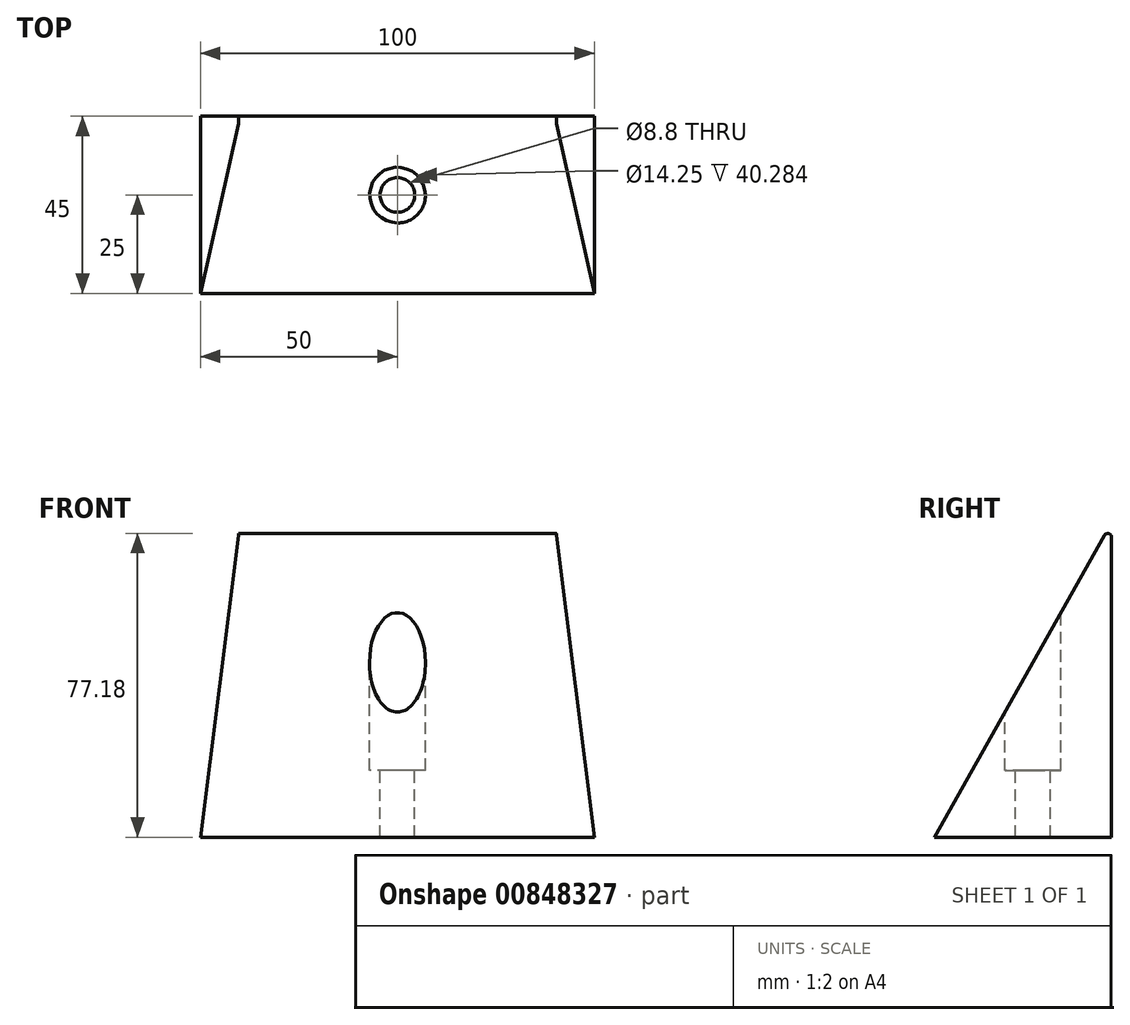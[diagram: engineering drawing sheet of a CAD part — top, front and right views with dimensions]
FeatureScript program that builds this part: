
annotation { "Feature Type Name" : "Feature", "Feature Type Description" : "" }
export const myFeature = defineFeature(function(context is Context, id is Id, definition is map)
    precondition{}
    {
        {
            var Q0;
            Q0=qCreatedBy(makeId("Front.planeOp"),FACE);
            var sketch = newSketch(context, id + "F0", { "sketchPlane" : qUnion([Q0])});
            skLineSegment(sketch, "E0", {"start": v(50, 0) * mm, "end": v(-50, 0) * mm});
            skLineSegment(sketch, "E1", {"start": v(-50, 0) * mm, "end": v(-40, 80) * mm});
            skLineSegment(sketch, "E2", {"start": v(-40, 80) * mm, "end": v(40, 80) * mm});
            skLineSegment(sketch, "E3", {"start": v(40, 80) * mm, "end": v(50, 0) * mm});
            skSolve(sketch);
        }
        {
            var Q0;
            Q0=makeQuery(id+"F0.imprint","IMPRINT",FACE,{"disambiguationData":[TD([[makeQuery(id+"F0.imprint","IMPRINT",EDGE,{"derivedFrom":sQuery(id+"F0.wireOp",EDGE,"E0")}),-1.0]])]});
            extrude(context, id + "F1", {"entities" : qUnion([Q0]), "depth" : 45 * mm, "offsetDistance" : 25 * mm});
        }
        {
            var Q0;
            Q0=qCreatedBy(makeId("Right.planeOp"),FACE);
            var sketch = newSketch(context, id + "F2", { "sketchPlane" : qUnion([Q0])});
            skLineSegment(sketch, "E4", {"start": v(0, 80) * mm, "end": v(-45, 80) * mm});
            skLineSegment(sketch, "E5", {"start": v(-45, 80) * mm, "end": v(-45, 0) * mm});
            skLineSegment(sketch, "E6", {"start": v(-45, 0) * mm, "end": v(0, 80) * mm});
            skSolve(sketch);
        }
        {
            var Q0;
            Q0 = qSketchRegion(id + "F2", true);
            extrude(context, id + "F3", {"entities" : qUnion([Q0]), "operationType" : NewBodyOperationType.REMOVE, "endBound" : BoundingType.THROUGH_ALL, "oppositeDirection" : true, "depth" : 25 * mm, "offsetDistance" : 25 * mm, "hasSecondDirection" : true, "secondDirectionBound" : SecondDirectionBoundingType.THROUGH_ALL, "secondDirectionOppositeDirection" : false, "secondDirectionDepth" : 25 * mm});
        }
        {
            var Q0;
            Q0=qCreatedBy(makeId("Top.planeOp"),FACE);
            cPlane(context, id + "F4", {"entities" : qUnion([Q0]), "cplaneType" : CPlaneType.OFFSET, "offset" : 25 * mm, "width" : 150 * mm, "height" : 150 * mm});
        }
        {
            var Q0;
            Q0=qCreatedBy(id+"F4.planeOp",FACE);
            var sketch = newSketch(context, id + "F5", { "sketchPlane" : qUnion([Q0])});
            skPoint(sketch, "E7", {"position": v(0, -20) * mm});
            skCircle(sketch, "E8", {"center": v(0, -20) * mm, "radius": 7.12 * mm});
            skSolve(sketch);
        }
        {
            var Q0;
            Q0=sQuery(id+"F5.wireOp",VERTEX,"E7");
            var Q1;
            Q1=makeQuery(id+"F1.opExtrude","SWEPT_BODY",BODY,{"disambiguationData":[OSD([sQuery(id+"F0.wireOp",EDGE,"E0"),sQuery(id+"F0.wireOp",EDGE,"E1"),sQuery(id+"F0.wireOp",EDGE,"E2"),sQuery(id+"F0.wireOp",EDGE,"E3")])]});
            hole(context, id + "F6", {"style" : HoleStyle.C_BORE, "endStyle" : HoleEndStyle.THROUGH, "standardTappedOrClearance" : lookupTablePath({ "fit" : "Normal", "standard" : "ISO", "size" : "M8", "type" : "Clearance" }), "standardBlindInLast" : lookupTablePath({ "fit" : "Standard", "standard" : "ISO", "size" : "M8", "type" : "Clearance" }), "holeDiameter" : 8.8 * mm, "cBoreDiameter" : 14.25 * mm, "cBoreDepth" : 8 * mm, "majorDiameter" : 5 * mm, "isTappedThrough" : true, "tappedDepth" : 12 * mm, "tapClearance" : 3, "startFromSketch" : true, "locations" : qUnion([Q0]), "scope" : qUnion([Q1])});
        }
        {
            var Q0;
            Q0 = qSketchRegion(id + "F5", true);
            extrude(context, id + "F7", {"entities" : qUnion([Q0]), "operationType" : NewBodyOperationType.REMOVE, "depth" : 80 * mm, "offsetDistance" : 25 * mm});
        }
        {
            var Q0;
            Q0=makeQuery(id+"F3.boolean.opBoolean","MERGE",EDGE,{"derivedFrom":[makeQuery(id+"F1.opExtrude","CAP_EDGE",EDGE,{"disambiguationData":[OSD([sQuery(id+"F0.wireOp",EDGE,"E2")])],"isStart":true}),makeQuery(id+"F3.opExtrude","SWEPT_EDGE",EDGE,{"disambiguationData":[OSD([sQuery(id+"F2.wireOp",EDGE,"E4"),sQuery(id+"F2.wireOp",EDGE,"E6")])]})]});
            fillet(context, id + "F8", {"entities" : qUnion([Q0]), "radius" : 1 * mm, "tangentPropagation" : true, "allowEdgeOverflow" : false});
        }
    });
